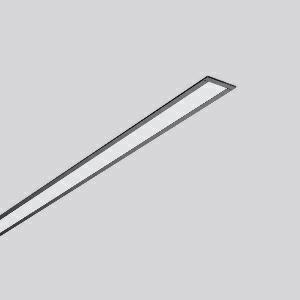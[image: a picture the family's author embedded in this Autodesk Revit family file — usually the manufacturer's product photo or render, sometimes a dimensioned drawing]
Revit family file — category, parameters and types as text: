
# Revit family: less_is_more_27_312176_003_1_76_2f76
name_source: partatom
category: Lighting Fixtures
units: mm (PartAtom-declared; Revit-internal decimal feet)

## family parameters
Cut with Voids When Loaded = No
Host = Face
Light Source = No
Part Type = Normal
Room Calculation Point = No
Round Connector Dimension = Use Diameter
Shared = No

## types (1)
- LESS IS MORE 27 (1 x LED Modul 840, 1600 lm, 4000)
    Apparent Load = 25 VA
    CIE Flux Codes = 48 79 96 100 100
    Color Rendering = 80
    Color Temperature = 4000
    Default Elevation = 1800 mm
    Description = Series: LESS IS MORE 27
Recessed ceiling and wall luminaire with slim design. Housing: extruded aluminium profile, powder-coated. End cap aluminium powder-coated. Diffuser made of non-yellowing plastic (PMMA), opal. Suitable for Recessed ceiling mounting, wall (recessed). External driver with connecting cable. 
Colour: deep black, matt (RAL 9005)
Length: 1014 mm
Width: 38 mm
Height: 2 mm
Cut-out length: 1006 mm
Cut-out width: 30 mm
Recess height: 45-60 mm
Luminaire: recess height: 37 mm
Lamp: LED
Socket: without socket
Colour temperature: 4000K
Colour rendering index (CRI): 82
System power: 25 W
Rated luminous flux: 1600 lm
Luminous efficiency: 64 lm/W
Control gear: Voltage converter, DALI dim.
Protection class: II
Type of protection: IP 20
    Height = 0 mm  [stored 0 ft]
    Lamp = 1 x LED Modul 840
    Lamp Light Flux = 1600 lm
    Lamp count = 1
    Length = 1014 mm
    Lifetime = 50000 h
    Luminous efficacy = 64 lm/W
    Manufacturer = RZB
    ModVariant = No
    Model = 312176.003.1.76
    Mounting Place = Ceiling, Wall
    Mounting Type = Recessed
    Number of Poles = 1
    OnlyDefault = Yes
    Power Factor = 1
    Product Name = LESS IS MORE 27
    Product group = Recessed LED linear luminaires
    ProductGroupID = 407
    Protection Class = Protection class II
    Protection Degree = IP 20
    RLX_Detail_Level = 1
    RLX_Emergency_Light_Flux = 0 lm
    RLX_Emergency_Type = 0
    RLX_Emergency_Type_DB = No
    RlxData = <blob elided: 26177 chars, md5=92f85285>
    Socket = socket
    Standby Power = 0 W
    System Light Flux = 1600 lm
    System Power = 25 W
    Type Comments = Product without accessories
    Type Image = 312176.003.jpg
    URL = http://relux.com
    VarID = ---
    Voltage = 230 V
    Voltage Range = 220-240 V
    Weight = 0.00 kg
    Width = 38 mm

note: [stored X ft] marks values corroborated as IEEE doubles in the binary element streams (Revit-internal decimal feet)

## geometry (parser evidence)
native form markers: Blend x4, Sweep x10
no freeform markers — native parametric forms only
